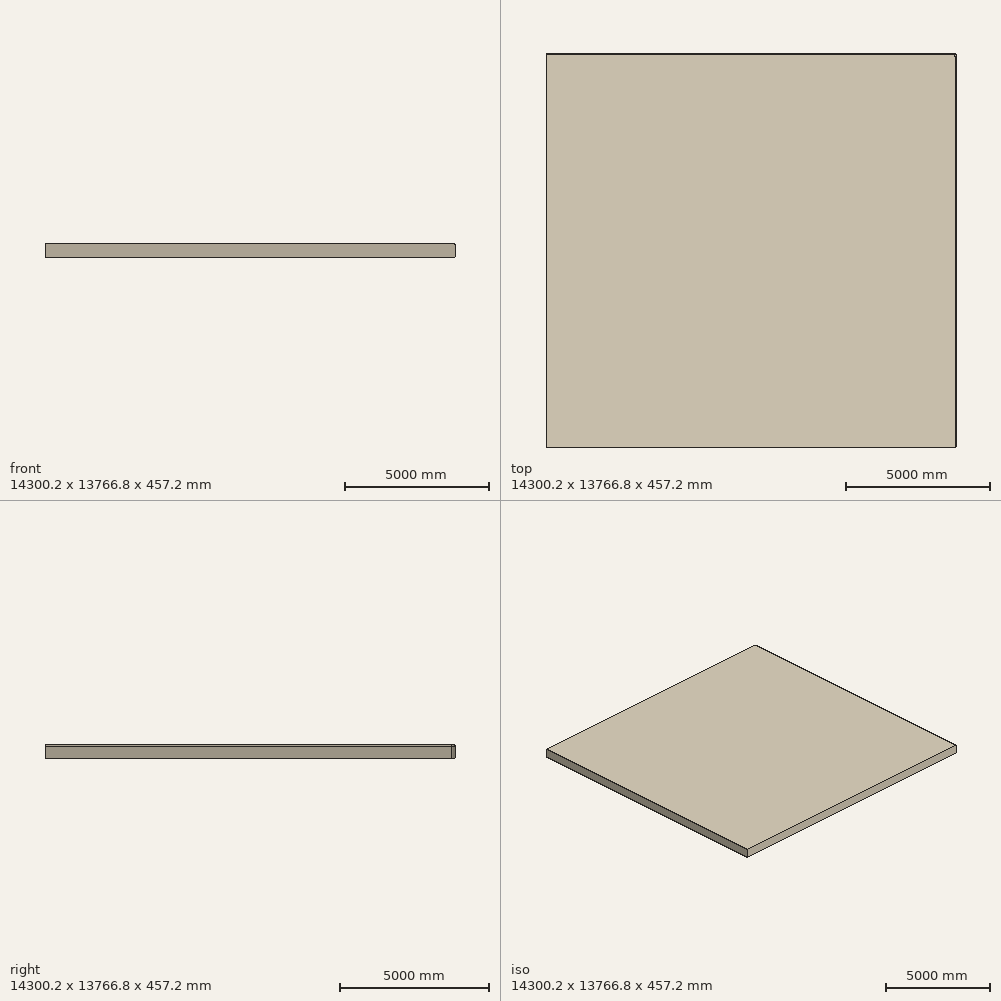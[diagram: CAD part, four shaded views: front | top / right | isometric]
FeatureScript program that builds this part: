
annotation { "Feature Type Name" : "Feature", "Feature Type Description" : "" }
export const myFeature = defineFeature(function(context is Context, id is Id, definition is map)
    precondition{}
    {
        {
            var Q0;
            Q0=qCreatedBy(makeId("Top.planeOp"),FACE);
            var sketch = newSketch(context, id + "F0", { "sketchPlane" : qUnion([Q0])});
            skLineSegment(sketch, "E0.bottom", {"start": v(-497.67, 0) * mm, "end": v(-14797.87, 0) * mm});
            skLineSegment(sketch, "E0.top", {"start": v(-497.67, -13766.8) * mm, "end": v(-14797.87, -13766.8) * mm});
            skLineSegment(sketch, "E0.left", {"start": v(-497.67, 0) * mm, "end": v(-497.67, -13766.8) * mm});
            skLineSegment(sketch, "E0.right", {"start": v(-14797.87, 0) * mm, "end": v(-14797.87, -13766.8) * mm});
            skSolve(sketch);
        }
        {
            var Q0;
            Q0 = qSketchRegion(id + "F0", true);
            extrude(context, id + "F1", {"entities" : qUnion([Q0]), "depth" : 457.2 * mm, "offsetDistance" : 25.4 * mm});
        }
        {
            var Q0;
            Q0=makeQuery(id+"F1.opExtrude","SWEPT_EDGE",EDGE,{"disambiguationData":[OSD([sQuery(id+"F0.wireOp",EDGE,"E0.bottom"),sQuery(id+"F0.wireOp",EDGE,"E0.left")])]});
            fillet(context, id + "F2", {"entities" : qUnion([Q0]), "radius" : 127 * mm, "tangentPropagation" : true, "allowEdgeOverflow" : false});
        }
        {
            var Q0;
            Q0=makeQuery(id+"F1.opExtrude","CAP_EDGE",EDGE,{"disambiguationData":[OSD([sQuery(id+"F0.wireOp",EDGE,"E0.left")])],"isStart":false});
            fillet(context, id + "F3", {"entities" : qUnion([Q0]), "radius" : 50.8 * mm, "tangentPropagation" : true, "allowEdgeOverflow" : false});
        }
    });
